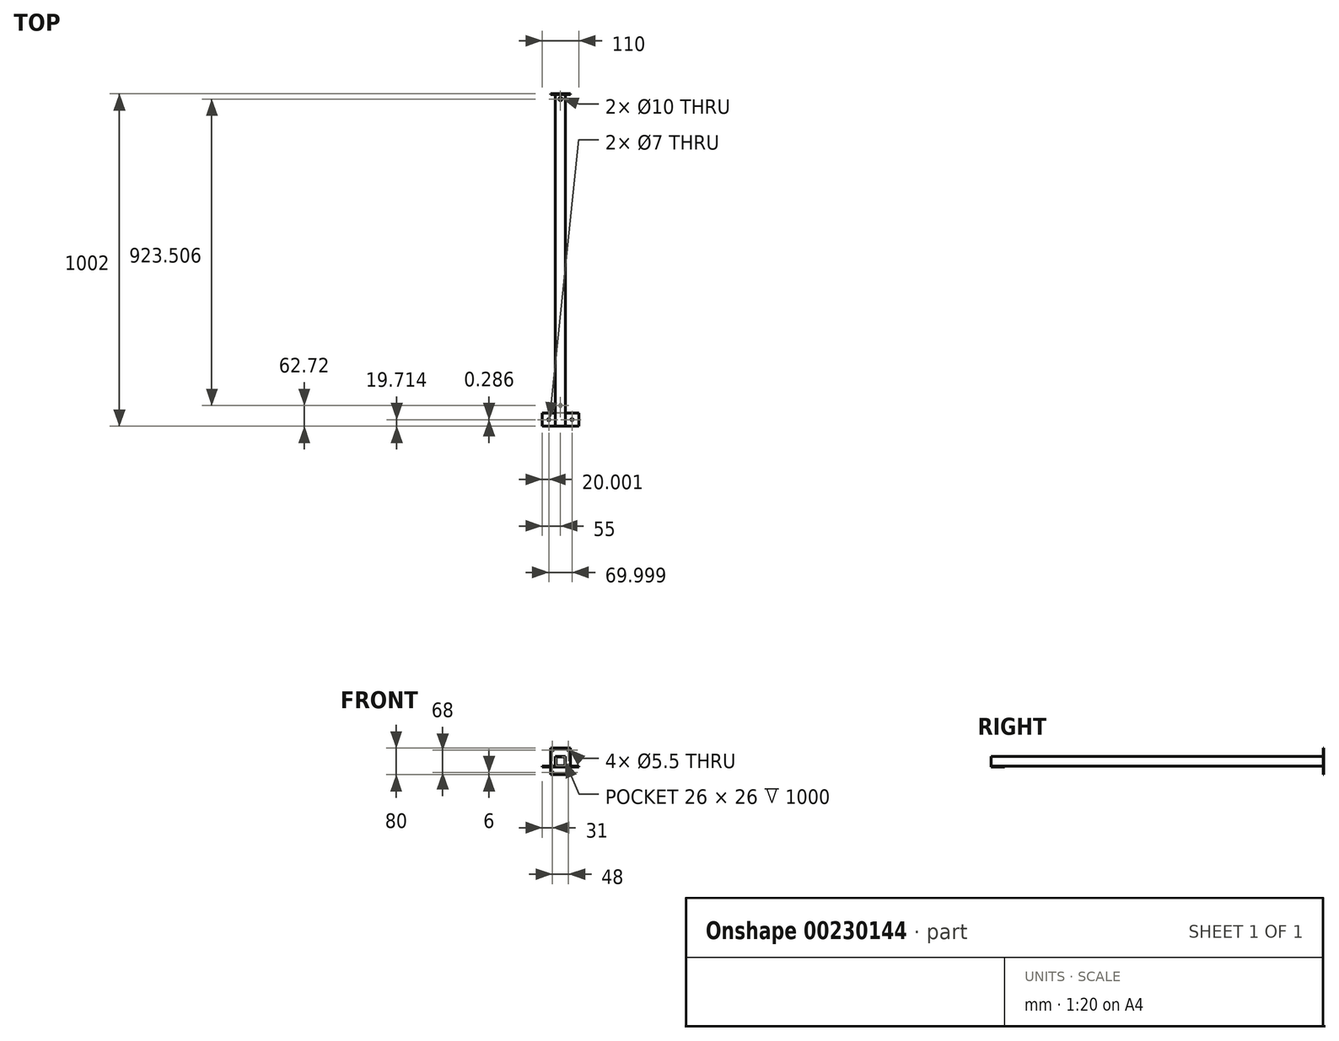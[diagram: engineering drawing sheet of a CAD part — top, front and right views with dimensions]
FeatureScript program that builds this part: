
annotation { "Feature Type Name" : "Feature", "Feature Type Description" : "" }
export const myFeature = defineFeature(function(context is Context, id is Id, definition is map)
    precondition{}
    {
        {
            var Q0;
            Q0=qCreatedBy(makeId("Front.planeOp"),FACE);
            var sketch = newSketch(context, id + "F0", { "sketchPlane" : qUnion([Q0])});
            skLineSegment(sketch, "E0.bottom", {"start": v(-30, 40) * mm, "end": v(30, 40) * mm});
            skLineSegment(sketch, "E0.top", {"start": v(-30, -40) * mm, "end": v(30, -40) * mm});
            skLineSegment(sketch, "E0.left", {"start": v(-30, 40) * mm, "end": v(-30, -40) * mm});
            skLineSegment(sketch, "E0.right", {"start": v(30, 40) * mm, "end": v(30, -40) * mm});
            skPoint(sketch, "E0.middle", {"position": v(0, 0) * mm});
            skCircle(sketch, "E1", {"center": v(-24, 34) * mm, "radius": 2.75 * mm});
            skCircle(sketch, "E2.MirrorC", {"center": v(24, 34) * mm, "radius": 2.75 * mm});
            skCircle(sketch, "E3.MirrorC", {"center": v(24, -34) * mm, "radius": 2.75 * mm});
            skCircle(sketch, "E4.MirrorC", {"center": v(-24, -34) * mm, "radius": 2.75 * mm});
            skSolve(sketch);
        }
        {
            var Q0;
            Q0 = qSketchRegion(id + "F0", true);
            extrude(context, id + "F1", {"entities" : qUnion([Q0]), "depth" : 2 * mm});
        }
        {
            var Q0;
            Q0=qCreatedBy(makeId("Front.planeOp"),FACE);
            var sketch = newSketch(context, id + "F2", { "sketchPlane" : qUnion([Q0])});
            skLineSegment(sketch, "E5.bottom", {"start": v(15, 15) * mm, "end": v(-15, 15) * mm});
            skLineSegment(sketch, "E5.top", {"start": v(15, -15) * mm, "end": v(-15, -15) * mm});
            skLineSegment(sketch, "E5.left", {"start": v(15, 15) * mm, "end": v(15, -15) * mm});
            skLineSegment(sketch, "E5.right", {"start": v(-15, 15) * mm, "end": v(-15, -15) * mm});
            skPoint(sketch, "E5.middle", {"position": v(0, 0) * mm});
            skLineSegment(sketch, "E6.bottom", {"start": v(13, -13) * mm, "end": v(-13, -13) * mm});
            skLineSegment(sketch, "E6.top", {"start": v(13, 13) * mm, "end": v(-13, 13) * mm});
            skLineSegment(sketch, "E6.left", {"start": v(13, -13) * mm, "end": v(13, 13) * mm});
            skLineSegment(sketch, "E6.right", {"start": v(-13, -13) * mm, "end": v(-13, 13) * mm});
            skSolve(sketch);
        }
        {
            var Q0;
            Q0 = qSketchRegion(id + "F2", true);
            extrude(context, id + "F3", {"entities" : qUnion([Q0]), "operationType" : NewBodyOperationType.ADD, "depth" : 1002 * mm});
        }
        {
            var Q0;
            Q0=makeQuery(id+"F3.opExtrude","SWEPT_FACE",FACE,{"disambiguationData":[OSD([sQuery(id+"F2.wireOp",EDGE,"E5.bottom")])]});
            var sketch = newSketch(context, id + "F4", { "sketchPlane" : qUnion([Q0])});
            skCircle(sketch, "E7", {"center": v(0, -15.77) * mm, "radius": 5 * mm});
            skSolve(sketch);
        }
        {
            var Q0;
            Q0 = qSketchRegion(id + "F4", true);
            extrude(context, id + "F5", {"entities" : qUnion([Q0]), "operationType" : NewBodyOperationType.REMOVE, "oppositeDirection" : true, "depth" : 5 * mm});
        }
        {
            var Q0;
            Q0=makeQuery(id+"F3.opExtrude","SWEPT_FACE",FACE,{"disambiguationData":[OSD([sQuery(id+"F2.wireOp",EDGE,"E5.top")])]});
            var sketch = newSketch(context, id + "F6", { "sketchPlane" : qUnion([Q0])});
            skLineSegment(sketch, "E8.bottom", {"start": v(55, 962) * mm, "end": v(-55, 962) * mm});
            skLineSegment(sketch, "E8.top", {"start": v(55, 1002) * mm, "end": v(-55, 1002) * mm});
            skLineSegment(sketch, "E8.left", {"start": v(55, 962) * mm, "end": v(55, 1002) * mm});
            skLineSegment(sketch, "E8.right", {"start": v(-55, 962) * mm, "end": v(-55, 1002) * mm});
            skCircle(sketch, "E9", {"center": v(35, 982) * mm, "radius": 3.5 * mm});
            skCircle(sketch, "E10.1.0.0", {"center": v(-35, 982.29) * mm, "radius": 3.5 * mm});
            skLineSegment(sketch, "E10.direction1", {"start": v(35, 982) * mm, "end": v(-35, 982.29) * mm, "construction": true});
            skCircle(sketch, "E11", {"center": v(0, 939.28) * mm, "radius": 5 * mm});
            skSolve(sketch);
        }
        {
            var Q0;
            {var subQ5=sQuery(id+"F6.wireOp",EDGE,"E8.left");Q0=makeQuery(id+"F6.imprint","IMPRINT",FACE,{"disambiguationData":[TD([[makeQuery(id+"F6.imprint","IMPRINT",EDGE,{"derivedFrom":subQ5}),1.0]])]});}
            var Q1;
            {var subQ0=sQuery(id+"F6.wireOp",EDGE,"E8.bottom");var subQ1=sQuery(id+"F2.wireOp",EDGE,"E5.top");var subQ2=makeQuery(id+"F3.opExtrude","SWEPT_EDGE",EDGE,{"disambiguationData":[OSD([subQ1,sQuery(id+"F2.wireOp",EDGE,"E5.left")])]});var subQ3=makeQuery(id+"F6.imprint","INTERSECT",VERTEX,{"derivedFrom":[subQ2,subQ0]});Q1=makeQuery(id+"F6.imprint","IMPRINT",FACE,{"disambiguationData":[TD([[makeQuery(id+"F6.imprint","IMPRINT",EDGE,{"disambiguationData":[TD([[subQ3,-1.0]])],"derivedFrom":subQ0}),-1.0]])]});}
            var Q2;
            {var subQ0=sQuery(id+"F6.wireOp",EDGE,"E8.right");Q2=makeQuery(id+"F6.imprint","IMPRINT",FACE,{"disambiguationData":[TD([[makeQuery(id+"F6.imprint","IMPRINT",EDGE,{"derivedFrom":subQ0}),-1.0]])]});}
            extrude(context, id + "F7", {"entities" : qUnion([Q0, Q1, Q2]), "operationType" : NewBodyOperationType.ADD, "depth" : 2 * mm});
        }
        {
            var Q0;
            Q0=makeQuery(id+"F6.imprint","IMPRINT",FACE,{"disambiguationData":[TD([[makeQuery(id+"F6.imprint","IMPRINT",EDGE,{"derivedFrom":sQuery(id+"F6.wireOp",EDGE,"E11")}),1.0]])]});
            var Q1;
            Q1=sQuery(id+"F6.wireOp",EDGE,"E11");
            extrude(context, id + "F8", {"entities" : qUnion([Q0]), "operationType" : NewBodyOperationType.REMOVE, "surfaceEntities" : qUnion([Q1]), "oppositeDirection" : true, "depth" : 5 * mm});
        }
    });
